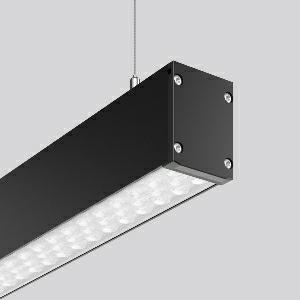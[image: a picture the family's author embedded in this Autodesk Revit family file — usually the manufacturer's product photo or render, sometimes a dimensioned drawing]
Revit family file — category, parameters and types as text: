
# Revit family: linedo_single_ip54_312566_003_76_3552
name_source: partatom
category: Lighting Fixtures
units: mm (PartAtom-declared; Revit-internal decimal feet)

## family parameters
Cut with Voids When Loaded = No
Host = Face
Light Source = No
Part Type = Normal
Room Calculation Point = No
Round Connector Dimension = Use Diameter
Shared = No

## types (1)
- LINEDO single IP54 (1 x LED Modul 830, 6100 lm, 3000)
    Apparent Load = 40 VA
    CIE Flux Codes = 86 96 99 100 100
    Color Rendering = 80
    Color Temperature = 3000
    Default Elevation = 1800 mm
    Description = Series: LINEDO single IP54
Stylish pendant luminaire. Housing: extruded aluminium profile, powder-coated. Plastic end caps, black. High-efficiency LED units with optimum light control thanks to clear plastic (PC) lens optics. 2-point steel cable suspension freely positionable and infinitely height-adjustable. With power cord (2.5 m). Please order canopy separately if required. Perfect for office areas (RUG < 19) and environments with computer screens in accordance with EN 12464-1. Luminaire with limited surface temperature in accordance with EN 60598-2-24 for use in environments in which a deposit of conductive dust on the luminaire can be expected. 
Colour: jet black (RAL 9005)
Length: 2274 mm
Width: 58 mm
Height: 76 mm
Suspension length: 100-1500 mm
Lamp: LED
Socket: without socket
Colour temperature: 3000K
Colour rendering index (CRI): 80
System power: 40 W
Rated luminous flux: 6100 lm
Beam angle Down: 59°
Luminous efficiency: 153 lm/W
Control gear: Converter, dimmable, DALI
Protection class: I
Type of protection: IP 54
    Height = 76 mm
    Lamp = 1 x LED Modul 830
    Lamp Light Flux = 6100 lm
    Lamp count = 1
    Length = 2274 mm
    Lifetime = 50000 h
    Luminous efficacy = 153 lm/W
    Manufacturer = RZB
    ModVariant = No
    Model = 312566.003.76
    Mounting Place = Ceiling
    Mounting Type = Surface mounted, Pendant
    Number of Poles = 1
    OnlyDefault = Yes
    Power Factor = 1
    Product Name = LINEDO single IP54
    Product group = Pendant luminaires
    ProductGroupID = 902
    Protection Class = Protection class I
    Protection Degree = IP 54
    RLX_Detail_Level = 1
    RLX_Emergency_Light_Flux = 0 lm
    RLX_Emergency_Type = 0
    RLX_Emergency_Type_DB = No
    RlxData = <blob elided: 35925 chars, md5=6eabfc79>
    Socket = socket
    Standby Power = 0 W
    System Light Flux = 6100 lm
    System Power = 40 W
    Type Comments = ALEA SPOT
    Type Image = 312565.003.jpg
    URL = http://relux.com
    VarID = ---
    Voltage = 230 V
    Voltage Range = 220-240 V
    Weight = 0.00 kg
    Width = 58 mm

## geometry (parser evidence)
native form markers: Blend x4, Sweep x9
no freeform markers — native parametric forms only
